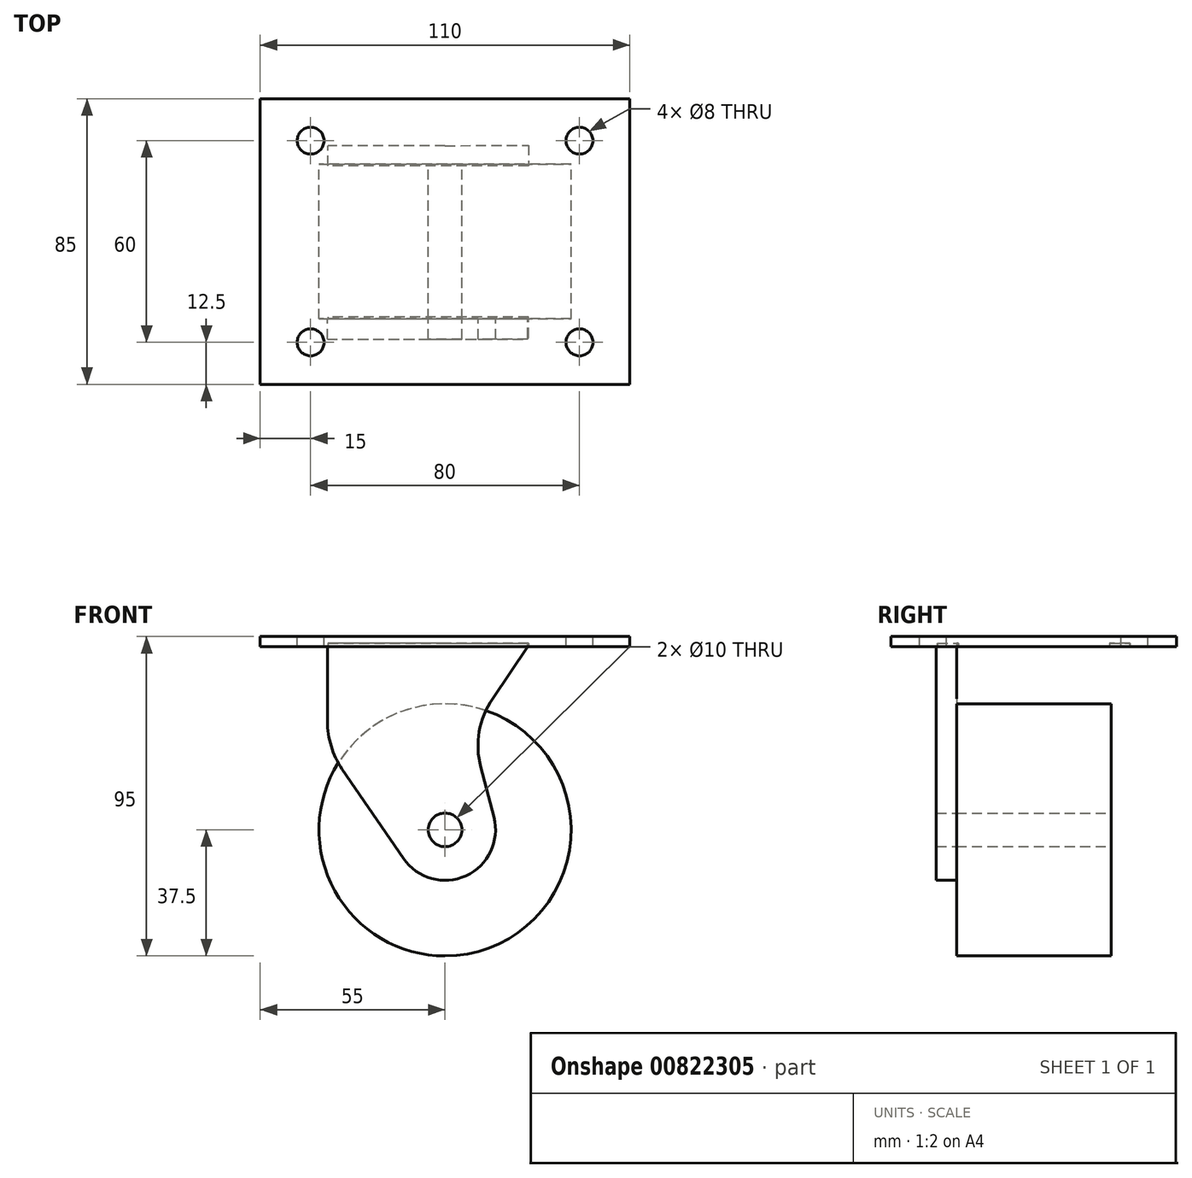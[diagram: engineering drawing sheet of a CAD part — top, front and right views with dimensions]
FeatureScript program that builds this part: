
annotation { "Feature Type Name" : "Feature", "Feature Type Description" : "" }
export const myFeature = defineFeature(function(context is Context, id is Id, definition is map)
    precondition{}
    {
        {
            var Q0;
            Q0=qCreatedBy(makeId("Front.planeOp"),FACE);
            var sketch = newSketch(context, id + "F0", { "sketchPlane" : qUnion([Q0])});
            skLineSegment(sketch, "E0", {"start": v(-100.47, 0) * mm, "end": v(-100.47, -95) * mm});
            skLineSegment(sketch, "E1", {"start": v(0, -95) * mm, "end": v(0, -57.5) * mm});
            skCircle(sketch, "E2", {"center": v(0, -57.5) * mm, "radius": 37.5 * mm});
            skCircle(sketch, "E3", {"center": v(0, -57.5) * mm, "radius": 5 * mm});
            skSolve(sketch);
        }
        {
            var Q0;
            Q0 = qSketchRegion(id + "F0", true);
            extrude(context, id + "F1", {"entities" : qUnion([Q0]), "depth" : 46 * mm, "offsetDistance" : 25 * mm, "symmetric" : true});
        }
        {
            var Q0;
            Q0=qCreatedBy(makeId("Top.planeOp"),FACE);
            var sketch = newSketch(context, id + "F2", { "sketchPlane" : qUnion([Q0])});
            skLineSegment(sketch, "E4.bottom", {"start": v(40, -30) * mm, "end": v(-40, -30) * mm});
            skLineSegment(sketch, "E4.top", {"start": v(40, 30) * mm, "end": v(-40, 30) * mm});
            skLineSegment(sketch, "E4.left", {"start": v(40, -30) * mm, "end": v(40, 30) * mm});
            skLineSegment(sketch, "E4.right", {"start": v(-40, -30) * mm, "end": v(-40, 30) * mm});
            skPoint(sketch, "E4.middle", {"position": v(0, 0) * mm});
            skLineSegment(sketch, "E5.bottom", {"start": v(55, -42.5) * mm, "end": v(-55, -42.5) * mm});
            skLineSegment(sketch, "E5.top", {"start": v(55, 42.5) * mm, "end": v(-55, 42.5) * mm});
            skLineSegment(sketch, "E5.left", {"start": v(55, -42.5) * mm, "end": v(55, 42.5) * mm});
            skLineSegment(sketch, "E5.right", {"start": v(-55, -42.5) * mm, "end": v(-55, 42.5) * mm});
            skCircle(sketch, "E6", {"center": v(40, 30) * mm, "radius": 4 * mm});
            skCircle(sketch, "E7", {"center": v(40, -30) * mm, "radius": 4 * mm});
            skCircle(sketch, "E8", {"center": v(-40, -30) * mm, "radius": 4 * mm});
            skCircle(sketch, "E9", {"center": v(-40, 30) * mm, "radius": 4 * mm});
            skSolve(sketch);
        }
        {
            var Q0;
            Q0 = qSketchRegion(id + "F2", true);
            var Q1;
            {var subQ5=sQuery(id+"F2.wireOp",EDGE,"E4.bottom");var subQ7=sQuery(id+"F2.wireOp",EDGE,"E7");var subQ15=makeQuery(id+"F2.imprint","INTERSECT",VERTEX,{"derivedFrom":[subQ5,subQ7]});Q1=makeQuery(id+"F2.imprint","IMPRINT",FACE,{"disambiguationData":[TD([[makeQuery(id+"F2.imprint","IMPRINT",EDGE,{"disambiguationData":[TD([[subQ15,-1.0]])],"derivedFrom":subQ5}),-1.0]])]});}
            extrude(context, id + "F3", {"entities" : qUnion([Q0, Q1]), "oppositeDirection" : true, "depth" : 3 * mm, "offsetDistance" : 25 * mm});
        }
        {
            var Q0;
            Q0=makeQuery(id+"F1.opExtrude","CAP_FACE",FACE,{"disambiguationData":[OSD([sQuery(id+"F0.wireOp",EDGE,"E2"),sQuery(id+"F0.wireOp",EDGE,"E3")])],"isStart":false});
            var sketch = newSketch(context, id + "F4", { "sketchPlane" : qUnion([Q0])});
            skCircle(sketch, "E10", {"center": v(0, -57.5) * mm, "radius": 5 * mm});
            skCircle(sketch, "E11", {"center": v(0, -57.5) * mm, "radius": 15 * mm});
            skLineSegment(sketch, "E12", {"start": v(0, 0) * mm, "end": v(0, -3) * mm});
            skLineSegment(sketch, "E13", {"start": v(0, -3) * mm, "end": v(-35, -3) * mm});
            skLineSegment(sketch, "E14", {"start": v(-35, -3) * mm, "end": v(-35, -25.25) * mm});
            skLineSegment(sketch, "E15", {"start": v(-30.61, -39.4) * mm, "end": v(-12.37, -65.99) * mm});
            skPoint(sketch, "E16.visualSharp", {"position": v(-35, -33) * mm});
            skArc(sketch, "E16.filletArc", {"start": v(-35, -25.25) * mm, "mid": v(-33.88, -32.65) * mm, "end": v(-30.61, -39.4) * mm});
            skLineSegment(sketch, "E17", {"start": v(0, -3) * mm, "end": v(24.58, -3) * mm});
            skLineSegment(sketch, "E18", {"start": v(24.58, -3) * mm, "end": v(14.11, -18.46) * mm});
            skLineSegment(sketch, "E19", {"start": v(10.62, -38.8) * mm, "end": v(14.51, -53.71) * mm});
            skPoint(sketch, "E20.visualSharp", {"position": v(7.76, -27.84) * mm});
            skArc(sketch, "E20.filletArc", {"start": v(14.11, -18.46) * mm, "mid": v(10.17, -28.25) * mm, "end": v(10.62, -38.8) * mm});
            skSolve(sketch);
        }
        {
            var Q0;
            Q0=makeQuery(id+"F4.imprint","IMPRINT",FACE,{"disambiguationData":[TD([[makeQuery(id+"F4.imprint","IMPRINT",EDGE,{"derivedFrom":sQuery(id+"F4.wireOp",EDGE,"E13")}),1.0]])]});
            var Q1;
            {var subQ1=sQuery(id+"F4.wireOp",EDGE,"E15");Q1=makeQuery(id+"F4.imprint","IMPRINT",FACE,{"disambiguationData":[TD([[makeQuery(id+"F4.imprint","IMPRINT",EDGE,{"derivedFrom":subQ1}),1.0]])]});}
            var Q2;
            Q2=makeQuery(id+"F4.imprint","IMPRINT",FACE,{"disambiguationData":[TD([[makeQuery(id+"F4.imprint","IMPRINT",EDGE,{"derivedFrom":sQuery(id+"F4.wireOp",EDGE,"E10")}),-1.0]])]});
            extrude(context, id + "F5", {"entities" : qUnion([Q0, Q1, Q2]), "depth" : 6 * mm, "offsetDistance" : 25 * mm});
        }
        {
            var Q0;
            Q0=makeQuery(id+"F3.opExtrude","CAP_FACE",FACE,{"disambiguationData":[OSD([sQuery(id+"F2.wireOp",EDGE,"E5.bottom"),sQuery(id+"F2.wireOp",EDGE,"E5.top"),sQuery(id+"F2.wireOp",EDGE,"E5.left"),sQuery(id+"F2.wireOp",EDGE,"E5.right"),sQuery(id+"F2.wireOp",EDGE,"E6"),sQuery(id+"F2.wireOp",EDGE,"E7"),sQuery(id+"F2.wireOp",EDGE,"E8"),sQuery(id+"F2.wireOp",EDGE,"E9")])],"isStart":false});
            var sketch = newSketch(context, id + "F6", { "sketchPlane" : qUnion([Q0])});
            skLineSegment(sketch, "E21", {"start": v(0, 0) * mm, "end": v(0, -22.5) * mm});
            skLineSegment(sketch, "E22", {"start": v(0, -22.5) * mm, "end": v(0, -28.5) * mm});
            skLineSegment(sketch, "E23", {"start": v(0, -28.5) * mm, "end": v(-34.78, -28.5) * mm});
            skLineSegment(sketch, "E24", {"start": v(24.8, -34.74) * mm, "end": v(24.8, -22.5) * mm});
            skLineSegment(sketch, "E25", {"start": v(24.8, -22.5) * mm, "end": v(0, -22.5) * mm});
            skLineSegment(sketch, "E26", {"start": v(0, -22.5) * mm, "end": v(-34.78, -22.5) * mm});
            skLineSegment(sketch, "E27", {"start": v(-34.78, -22.5) * mm, "end": v(-34.78, -28.5) * mm});
            skLineSegment(sketch, "E28", {"start": v(0, -28.5) * mm, "end": v(24.8, -28.62) * mm});
            skLineSegment(sketch, "E29", {"start": v(0, 0) * mm, "end": v(26.03, 0) * mm});
            skLineSegment(sketch, "E30.MirrorCS", {"start": v(24.8, 22.5) * mm, "end": v(0, 22.5) * mm});
            skLineSegment(sketch, "E31.MirrorCS", {"start": v(0, 22.5) * mm, "end": v(-34.78, 22.5) * mm});
            skLineSegment(sketch, "E32.MirrorCS", {"start": v(0, 28.5) * mm, "end": v(-34.78, 28.5) * mm});
            skLineSegment(sketch, "E33.MirrorCS", {"start": v(0, 28.5) * mm, "end": v(24.8, 28.62) * mm});
            skLineSegment(sketch, "E34.MirrorCS", {"start": v(-34.78, 22.5) * mm, "end": v(-34.78, 28.5) * mm});
            skLineSegment(sketch, "E35.MirrorCS", {"start": v(24.8, 34.74) * mm, "end": v(24.8, 22.5) * mm});
            skSolve(sketch);
        }
        {
            var Q0;
            Q0 = qSketchRegion(id + "F6", true);
            extrude(context, id + "F7", {"entities" : qUnion([Q0]), "operationType" : NewBodyOperationType.REMOVE, "oppositeDirection" : true, "depth" : 1 * mm, "offsetDistance" : 25 * mm});
        }
        {
            var Q0;
            Q0=makeQuery(id+"F5.opExtrude","SWEPT_FACE",FACE,{"disambiguationData":[OSD([sQuery(id+"F4.wireOp",EDGE,"E13"),sQuery(id+"F4.wireOp",EDGE,"E17")])]});
            extrude(context, id + "F8", {"entities" : qUnion([Q0]), "operationType" : NewBodyOperationType.ADD, "depth" : 1 * mm, "offsetDistance" : 25 * mm});
        }
    });
